# Revit family: Midmark - CM Dry Exam Lift Table
name_source: partatom
category: Specialty Equipment
revit_build: Autodesk Revit 2017 (Build: 20190507_1515(x64)
units: mm (PartAtom-declared; Revit-internal decimal feet)

## family parameters
Always vertical = Yes
Cut with Voids When Loaded = No
OmniClass Number = 23.25.61.00
Part Type = Normal
Room Calculation Point = No
Round Connector Dimension = Use Diameter
Shared = No
Work Plane-Based = No

## types (2) — shared parameters
Base & Lift Column Material = Steel, Paint Finish, Midmark - Pebble Grey
Depth = 4' - 7 1/2"
Height = 3' - 0"
Manufacturer = MIDMARK
Scale Monitor Material = Plastic, Opaque Black
Table Pad Material = Vynil Fabric, Green
Table Top Material = Stainless Steel, Polished
Width = 2' - 1 1/2"
zero-valued in all types: Weight

## per-type parameters (varying)
| type | Model | No Scale | Scale | Type Comments |
| Lift Table without Scale | CMWO | Yes | No | CM Dry Exam Lift Table.  Connection Power - 115V AC, 60 Hz, 10 AMP |
| Lift Table with Scale | CMWS | No | Yes | CM Dry Exam Lift Table with Scale.  Connection Power - 115V AC, 60 Hz, 10 AMP |

## geometry (parser evidence)
native form markers: Sweep x2
no freeform markers — native parametric forms only
